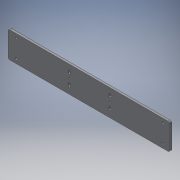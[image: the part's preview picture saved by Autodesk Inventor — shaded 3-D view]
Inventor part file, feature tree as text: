
AUTODESK INVENTOR PART (.ipt)
format: ipt  version: 2019 (Build 230136000, 136)  size: 160,256 bytes
history: native  units: in
note: dims shown in document units (in); Inventor stores cm internally (conversion verified against a paired STEP export)
features: reference x12, other x6, extrude x3, sketch x3, fillet x1, helix x1
ambient origin geometry x8: Origin, YZ Plane, XZ Plane, XY Plane, X Axis, Y Axis, Z Axis, Center Point
bodies: Solid1 (feature_tree)
feature tree (26):
  extrude  "Extrusion1"  Depth=0.1575in TaperAngle=0.0deg
  fillet  "Fillet1"  Radius=0.125in
  extrude  "Extrusion2"  Depth=0.0039in
  extrude  "Extrusion3"  Depth=0.1575in
  sketch  "Sketch1"  dims[d0=1.9685in d1=0.1575in d2=0.0in d3=0.125in]
  reference  "Reference1"
  reference  "Reference2"
  sketch  "Sketch2"  dims[d4=0.0039in d5=0.0039in]
  reference  "Reference3"
  reference  "Reference4"
  reference  "Reference5"
  reference  "Reference6"
  reference  "Reference7"
  reference  "Reference8"
  reference  "Reference9"
  reference  "Reference10"
  sketch  "Sketch3"  dims[d6=0.0039in d7=0.0039in d8=0.1181in d9=0.1181in d10=0.1575in d11=0.0in d12=0.315in d13=0.315in d14=0.1575in d15=0.1575in d16=0.1575in d17=0.1575in d18=0.1575in d19=0.0in]
  reference  "Reference11"
  reference  "Reference12"
  other  "<userpath>\Documents\CAD Files\Helix DLP\Helix DLP.iam"
  helix  "Helix DLP.iam"  [1 undecoded]
  other  "30X30 - T-slot - Aluminium Profile:1"
  other  "30X30 - T-slot - Aluminium Profile:2"
  other  "motor_brace_3:2"
  other  "motor_brace_3:1"
  other  "M1173041- NEMA 17 Screw rod:1"
note: 1 required parameter value undecoded (feature->parameter linkage not recoverable at this tier; creation-order binding heuristic only, values carry confidence <= 0.55)
